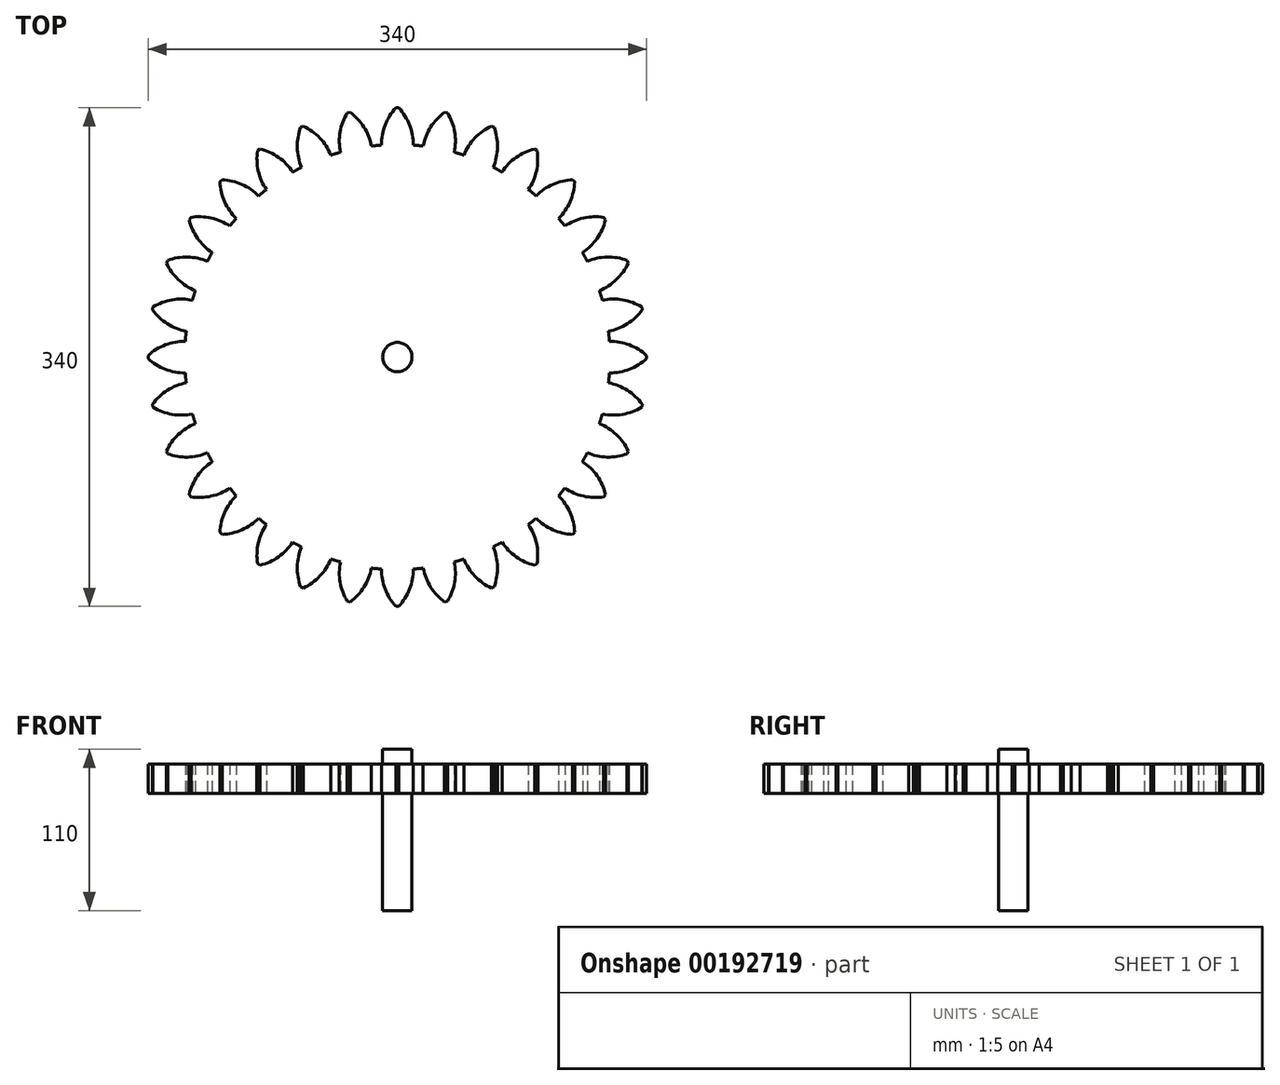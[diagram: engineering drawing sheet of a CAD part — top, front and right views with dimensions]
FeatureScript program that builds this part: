
annotation { "Feature Type Name" : "Feature", "Feature Type Description" : "" }
export const myFeature = defineFeature(function(context is Context, id is Id, definition is map)
    precondition{}
    {
        {
            var Q0;
            Q0=qCreatedBy(makeId("Top.planeOp"),FACE);
            var sketch = newSketch(context, id + "F0", { "sketchPlane" : qUnion([Q0])});
            skCircle(sketch, "E0", {"center": v(0, 0) * mm, "radius": 145 * mm});
            skLineSegment(sketch, "E1", {"start": v(0, 0) * mm, "end": v(0, 145) * mm, "construction": true});
            skLineSegment(sketch, "E2", {"start": v(0, 145) * mm, "end": v(0, 170) * mm});
            skLineSegment(sketch, "E3", {"start": v(0, 170) * mm, "end": v(-1, 170) * mm});
            skArc(sketch, "E4", {"start": v(-1, 170) * mm, "mid": v(-8.33, 158.24) * mm, "end": v(-10.8, 144.6) * mm});
            skLineSegment(sketch, "E5.MirrorCS", {"start": v(0, 170) * mm, "end": v(1, 170) * mm});
            skArc(sketch, "E6.MirrorCS", {"start": v(1, 170) * mm, "mid": v(8.33, 158.24) * mm, "end": v(10.8, 144.6) * mm});
            skArc(sketch, "E7.1.0", {"start": v(-34.15, 166.54) * mm, "mid": v(-39.04, 153.57) * mm, "end": v(-38.8, 139.71) * mm});
            skLineSegment(sketch, "E7.1.1", {"start": v(-33.17, 166.73) * mm, "end": v(-34.15, 166.54) * mm});
            skLineSegment(sketch, "E7.1.2", {"start": v(-33.17, 166.73) * mm, "end": v(-32.18, 166.93) * mm});
            skArc(sketch, "E7.1.3", {"start": v(-32.18, 166.93) * mm, "mid": v(-22.7, 156.82) * mm, "end": v(-17.62, 143.93) * mm});
            skArc(sketch, "E7.2.0", {"start": v(-65.98, 156.68) * mm, "mid": v(-68.25, 143) * mm, "end": v(-65.3, 129.46) * mm});
            skLineSegment(sketch, "E7.2.1", {"start": v(-65.06, 157.06) * mm, "end": v(-65.98, 156.68) * mm});
            skLineSegment(sketch, "E7.2.2", {"start": v(-65.06, 157.06) * mm, "end": v(-64.13, 157.44) * mm});
            skArc(sketch, "E7.2.3", {"start": v(-64.13, 157.44) * mm, "mid": v(-52.86, 149.38) * mm, "end": v(-45.36, 137.72) * mm});
            skArc(sketch, "E7.3.0", {"start": v(-95.28, 140.8) * mm, "mid": v(-94.84, 126.94) * mm, "end": v(-89.3, 114.23) * mm});
            skLineSegment(sketch, "E7.3.1", {"start": v(-94.45, 141.35) * mm, "end": v(-95.28, 140.8) * mm});
            skLineSegment(sketch, "E7.3.2", {"start": v(-94.45, 141.35) * mm, "end": v(-93.62, 141.9) * mm});
            skArc(sketch, "E7.3.3", {"start": v(-93.62, 141.9) * mm, "mid": v(-80.98, 136.2) * mm, "end": v(-71.36, 126.23) * mm});
            skArc(sketch, "E7.4.0", {"start": v(-120.92, 119.5) * mm, "mid": v(-117.78, 106) * mm, "end": v(-109.88, 94.61) * mm});
            skLineSegment(sketch, "E7.4.1", {"start": v(-120.2, 120.2) * mm, "end": v(-120.92, 119.5) * mm});
            skLineSegment(sketch, "E7.4.2", {"start": v(-120.2, 120.2) * mm, "end": v(-119.5, 120.92) * mm});
            skArc(sketch, "E7.4.3", {"start": v(-119.5, 120.92) * mm, "mid": v(-106, 117.78) * mm, "end": v(-94.61, 109.88) * mm});
            skArc(sketch, "E7.5.0", {"start": v(-141.9, 93.62) * mm, "mid": v(-136.2, 80.98) * mm, "end": v(-126.23, 71.36) * mm});
            skLineSegment(sketch, "E7.5.1", {"start": v(-141.35, 94.45) * mm, "end": v(-141.9, 93.62) * mm});
            skLineSegment(sketch, "E7.5.2", {"start": v(-141.35, 94.45) * mm, "end": v(-140.8, 95.28) * mm});
            skArc(sketch, "E7.5.3", {"start": v(-140.8, 95.28) * mm, "mid": v(-126.94, 94.84) * mm, "end": v(-114.23, 89.3) * mm});
            skArc(sketch, "E7.6.0", {"start": v(-157.44, 64.13) * mm, "mid": v(-149.38, 52.86) * mm, "end": v(-137.72, 45.36) * mm});
            skLineSegment(sketch, "E7.6.1", {"start": v(-157.06, 65.06) * mm, "end": v(-157.44, 64.13) * mm});
            skLineSegment(sketch, "E7.6.2", {"start": v(-157.06, 65.06) * mm, "end": v(-156.68, 65.98) * mm});
            skArc(sketch, "E7.6.3", {"start": v(-156.68, 65.98) * mm, "mid": v(-143, 68.25) * mm, "end": v(-129.46, 65.3) * mm});
            skArc(sketch, "E7.7.0", {"start": v(-166.93, 32.18) * mm, "mid": v(-156.82, 22.7) * mm, "end": v(-143.93, 17.62) * mm});
            skLineSegment(sketch, "E7.7.1", {"start": v(-166.73, 33.17) * mm, "end": v(-166.93, 32.18) * mm});
            skLineSegment(sketch, "E7.7.2", {"start": v(-166.73, 33.17) * mm, "end": v(-166.54, 34.15) * mm});
            skArc(sketch, "E7.7.3", {"start": v(-166.54, 34.15) * mm, "mid": v(-153.57, 39.04) * mm, "end": v(-139.71, 38.8) * mm});
            skArc(sketch, "E8.3.8.0", {"start": v(-170, -1) * mm, "mid": v(-158.24, -8.33) * mm, "end": v(-144.6, -10.8) * mm});
            skLineSegment(sketch, "E8.4.8.0", {"start": v(-170, 0) * mm, "end": v(-170, -1) * mm});
            skLineSegment(sketch, "E8.7.8.0", {"start": v(-170, 0) * mm, "end": v(-170, 1) * mm});
            skArc(sketch, "E8.10.8.0", {"start": v(-170, 1) * mm, "mid": v(-158.24, 8.33) * mm, "end": v(-144.6, 10.8) * mm});
            skArc(sketch, "E8.3.9.0", {"start": v(-166.54, -34.15) * mm, "mid": v(-153.57, -39.04) * mm, "end": v(-139.71, -38.8) * mm});
            skLineSegment(sketch, "E8.4.9.0", {"start": v(-166.73, -33.17) * mm, "end": v(-166.54, -34.15) * mm});
            skLineSegment(sketch, "E8.7.9.0", {"start": v(-166.73, -33.17) * mm, "end": v(-166.93, -32.18) * mm});
            skArc(sketch, "E8.10.9.0", {"start": v(-166.93, -32.18) * mm, "mid": v(-156.82, -22.7) * mm, "end": v(-143.93, -17.62) * mm});
            skArc(sketch, "E9.3.10.0", {"start": v(-156.68, -65.98) * mm, "mid": v(-143, -68.25) * mm, "end": v(-129.46, -65.3) * mm});
            skLineSegment(sketch, "E9.4.10.0", {"start": v(-157.06, -65.06) * mm, "end": v(-156.68, -65.98) * mm});
            skLineSegment(sketch, "E9.7.10.0", {"start": v(-157.06, -65.06) * mm, "end": v(-157.44, -64.13) * mm});
            skArc(sketch, "E9.10.10.0", {"start": v(-157.44, -64.13) * mm, "mid": v(-149.38, -52.86) * mm, "end": v(-137.72, -45.36) * mm});
            skArc(sketch, "E9.3.11.0", {"start": v(-140.8, -95.28) * mm, "mid": v(-126.94, -94.84) * mm, "end": v(-114.23, -89.3) * mm});
            skLineSegment(sketch, "E9.4.11.0", {"start": v(-141.35, -94.45) * mm, "end": v(-140.8, -95.28) * mm});
            skLineSegment(sketch, "E9.7.11.0", {"start": v(-141.35, -94.45) * mm, "end": v(-141.9, -93.62) * mm});
            skArc(sketch, "E9.10.11.0", {"start": v(-141.9, -93.62) * mm, "mid": v(-136.2, -80.98) * mm, "end": v(-126.23, -71.36) * mm});
            skArc(sketch, "E9.3.12.0", {"start": v(-119.5, -120.92) * mm, "mid": v(-106, -117.78) * mm, "end": v(-94.61, -109.88) * mm});
            skLineSegment(sketch, "E9.4.12.0", {"start": v(-120.2, -120.2) * mm, "end": v(-119.5, -120.92) * mm});
            skLineSegment(sketch, "E9.7.12.0", {"start": v(-120.2, -120.2) * mm, "end": v(-120.92, -119.5) * mm});
            skArc(sketch, "E9.10.12.0", {"start": v(-120.92, -119.5) * mm, "mid": v(-117.78, -106) * mm, "end": v(-109.88, -94.61) * mm});
            skArc(sketch, "E9.3.13.0", {"start": v(-93.62, -141.9) * mm, "mid": v(-80.98, -136.2) * mm, "end": v(-71.36, -126.23) * mm});
            skLineSegment(sketch, "E9.4.13.0", {"start": v(-94.45, -141.35) * mm, "end": v(-93.62, -141.9) * mm});
            skLineSegment(sketch, "E9.7.13.0", {"start": v(-94.45, -141.35) * mm, "end": v(-95.28, -140.8) * mm});
            skArc(sketch, "E9.10.13.0", {"start": v(-95.28, -140.8) * mm, "mid": v(-94.84, -126.94) * mm, "end": v(-89.3, -114.23) * mm});
            skArc(sketch, "E9.3.14.0", {"start": v(-64.13, -157.44) * mm, "mid": v(-52.86, -149.38) * mm, "end": v(-45.36, -137.72) * mm});
            skLineSegment(sketch, "E9.4.14.0", {"start": v(-65.06, -157.06) * mm, "end": v(-64.13, -157.44) * mm});
            skLineSegment(sketch, "E9.7.14.0", {"start": v(-65.06, -157.06) * mm, "end": v(-65.98, -156.68) * mm});
            skArc(sketch, "E9.10.14.0", {"start": v(-65.98, -156.68) * mm, "mid": v(-68.25, -143) * mm, "end": v(-65.3, -129.46) * mm});
            skArc(sketch, "E9.3.15.0", {"start": v(-32.18, -166.93) * mm, "mid": v(-22.7, -156.82) * mm, "end": v(-17.62, -143.93) * mm});
            skLineSegment(sketch, "E9.4.15.0", {"start": v(-33.17, -166.73) * mm, "end": v(-32.18, -166.93) * mm});
            skLineSegment(sketch, "E9.7.15.0", {"start": v(-33.17, -166.73) * mm, "end": v(-34.15, -166.54) * mm});
            skArc(sketch, "E9.10.15.0", {"start": v(-34.15, -166.54) * mm, "mid": v(-39.04, -153.57) * mm, "end": v(-38.8, -139.71) * mm});
            skArc(sketch, "E9.3.16.0", {"start": v(1, -170) * mm, "mid": v(8.33, -158.24) * mm, "end": v(10.8, -144.6) * mm});
            skLineSegment(sketch, "E9.4.16.0", {"start": v(0, -170) * mm, "end": v(1, -170) * mm});
            skLineSegment(sketch, "E9.7.16.0", {"start": v(0, -170) * mm, "end": v(-1, -170) * mm});
            skArc(sketch, "E9.10.16.0", {"start": v(-1, -170) * mm, "mid": v(-8.33, -158.24) * mm, "end": v(-10.8, -144.6) * mm});
            skArc(sketch, "E9.3.17.0", {"start": v(34.15, -166.54) * mm, "mid": v(39.04, -153.57) * mm, "end": v(38.8, -139.71) * mm});
            skLineSegment(sketch, "E9.4.17.0", {"start": v(33.17, -166.73) * mm, "end": v(34.15, -166.54) * mm});
            skLineSegment(sketch, "E9.7.17.0", {"start": v(33.17, -166.73) * mm, "end": v(32.18, -166.93) * mm});
            skArc(sketch, "E9.10.17.0", {"start": v(32.18, -166.93) * mm, "mid": v(22.7, -156.82) * mm, "end": v(17.62, -143.93) * mm});
            skArc(sketch, "E9.3.18.0", {"start": v(65.98, -156.68) * mm, "mid": v(68.25, -143) * mm, "end": v(65.3, -129.46) * mm});
            skLineSegment(sketch, "E9.4.18.0", {"start": v(65.06, -157.06) * mm, "end": v(65.98, -156.68) * mm});
            skLineSegment(sketch, "E9.7.18.0", {"start": v(65.06, -157.06) * mm, "end": v(64.13, -157.44) * mm});
            skArc(sketch, "E9.10.18.0", {"start": v(64.13, -157.44) * mm, "mid": v(52.86, -149.38) * mm, "end": v(45.36, -137.72) * mm});
            skArc(sketch, "E9.3.19.0", {"start": v(95.28, -140.8) * mm, "mid": v(94.84, -126.94) * mm, "end": v(89.3, -114.23) * mm});
            skLineSegment(sketch, "E9.4.19.0", {"start": v(94.45, -141.35) * mm, "end": v(95.28, -140.8) * mm});
            skLineSegment(sketch, "E9.7.19.0", {"start": v(94.45, -141.35) * mm, "end": v(93.62, -141.9) * mm});
            skArc(sketch, "E9.10.19.0", {"start": v(93.62, -141.9) * mm, "mid": v(80.98, -136.2) * mm, "end": v(71.36, -126.23) * mm});
            skArc(sketch, "E9.3.20.0", {"start": v(120.92, -119.5) * mm, "mid": v(117.78, -106) * mm, "end": v(109.88, -94.61) * mm});
            skLineSegment(sketch, "E9.4.20.0", {"start": v(120.2, -120.2) * mm, "end": v(120.92, -119.5) * mm});
            skLineSegment(sketch, "E9.7.20.0", {"start": v(120.2, -120.2) * mm, "end": v(119.5, -120.92) * mm});
            skArc(sketch, "E9.10.20.0", {"start": v(119.5, -120.92) * mm, "mid": v(106, -117.78) * mm, "end": v(94.61, -109.88) * mm});
            skArc(sketch, "E9.3.21.0", {"start": v(141.9, -93.62) * mm, "mid": v(136.2, -80.98) * mm, "end": v(126.23, -71.36) * mm});
            skLineSegment(sketch, "E9.4.21.0", {"start": v(141.35, -94.45) * mm, "end": v(141.9, -93.62) * mm});
            skLineSegment(sketch, "E9.7.21.0", {"start": v(141.35, -94.45) * mm, "end": v(140.8, -95.28) * mm});
            skArc(sketch, "E9.10.21.0", {"start": v(140.8, -95.28) * mm, "mid": v(126.94, -94.84) * mm, "end": v(114.23, -89.3) * mm});
            skArc(sketch, "E9.3.22.0", {"start": v(157.44, -64.13) * mm, "mid": v(149.38, -52.86) * mm, "end": v(137.72, -45.36) * mm});
            skLineSegment(sketch, "E9.4.22.0", {"start": v(157.06, -65.06) * mm, "end": v(157.44, -64.13) * mm});
            skLineSegment(sketch, "E9.7.22.0", {"start": v(157.06, -65.06) * mm, "end": v(156.68, -65.98) * mm});
            skArc(sketch, "E9.10.22.0", {"start": v(156.68, -65.98) * mm, "mid": v(143, -68.25) * mm, "end": v(129.46, -65.3) * mm});
            skArc(sketch, "E9.3.23.0", {"start": v(166.93, -32.18) * mm, "mid": v(156.82, -22.7) * mm, "end": v(143.93, -17.62) * mm});
            skLineSegment(sketch, "E9.4.23.0", {"start": v(166.73, -33.17) * mm, "end": v(166.93, -32.18) * mm});
            skLineSegment(sketch, "E9.7.23.0", {"start": v(166.73, -33.17) * mm, "end": v(166.54, -34.15) * mm});
            skArc(sketch, "E9.10.23.0", {"start": v(166.54, -34.15) * mm, "mid": v(153.57, -39.04) * mm, "end": v(139.71, -38.8) * mm});
            skArc(sketch, "E9.3.24.0", {"start": v(170, 1) * mm, "mid": v(158.24, 8.33) * mm, "end": v(144.6, 10.8) * mm});
            skLineSegment(sketch, "E9.4.24.0", {"start": v(170, 0) * mm, "end": v(170, 1) * mm});
            skLineSegment(sketch, "E9.7.24.0", {"start": v(170, 0) * mm, "end": v(170, -1) * mm});
            skArc(sketch, "E9.10.24.0", {"start": v(170, -1) * mm, "mid": v(158.24, -8.33) * mm, "end": v(144.6, -10.8) * mm});
            skArc(sketch, "E9.3.25.0", {"start": v(166.54, 34.15) * mm, "mid": v(153.57, 39.04) * mm, "end": v(139.71, 38.8) * mm});
            skLineSegment(sketch, "E9.4.25.0", {"start": v(166.73, 33.17) * mm, "end": v(166.54, 34.15) * mm});
            skLineSegment(sketch, "E9.7.25.0", {"start": v(166.73, 33.17) * mm, "end": v(166.93, 32.18) * mm});
            skArc(sketch, "E9.10.25.0", {"start": v(166.93, 32.18) * mm, "mid": v(156.82, 22.7) * mm, "end": v(143.93, 17.62) * mm});
            skArc(sketch, "E9.3.26.0", {"start": v(156.68, 65.98) * mm, "mid": v(143, 68.25) * mm, "end": v(129.46, 65.3) * mm});
            skLineSegment(sketch, "E9.4.26.0", {"start": v(157.06, 65.06) * mm, "end": v(156.68, 65.98) * mm});
            skLineSegment(sketch, "E9.7.26.0", {"start": v(157.06, 65.06) * mm, "end": v(157.44, 64.13) * mm});
            skArc(sketch, "E9.10.26.0", {"start": v(157.44, 64.13) * mm, "mid": v(149.38, 52.86) * mm, "end": v(137.72, 45.36) * mm});
            skArc(sketch, "E9.3.27.0", {"start": v(140.8, 95.28) * mm, "mid": v(126.94, 94.84) * mm, "end": v(114.23, 89.3) * mm});
            skLineSegment(sketch, "E9.4.27.0", {"start": v(141.35, 94.45) * mm, "end": v(140.8, 95.28) * mm});
            skLineSegment(sketch, "E9.7.27.0", {"start": v(141.35, 94.45) * mm, "end": v(141.9, 93.62) * mm});
            skArc(sketch, "E9.10.27.0", {"start": v(141.9, 93.62) * mm, "mid": v(136.2, 80.98) * mm, "end": v(126.23, 71.36) * mm});
            skArc(sketch, "E9.3.28.0", {"start": v(119.5, 120.92) * mm, "mid": v(106, 117.78) * mm, "end": v(94.61, 109.88) * mm});
            skLineSegment(sketch, "E9.4.28.0", {"start": v(120.2, 120.2) * mm, "end": v(119.5, 120.92) * mm});
            skLineSegment(sketch, "E9.7.28.0", {"start": v(120.2, 120.2) * mm, "end": v(120.92, 119.5) * mm});
            skArc(sketch, "E9.10.28.0", {"start": v(120.92, 119.5) * mm, "mid": v(117.78, 106) * mm, "end": v(109.88, 94.61) * mm});
            skArc(sketch, "E9.3.29.0", {"start": v(93.62, 141.9) * mm, "mid": v(80.98, 136.2) * mm, "end": v(71.36, 126.23) * mm});
            skLineSegment(sketch, "E9.4.29.0", {"start": v(94.45, 141.35) * mm, "end": v(93.62, 141.9) * mm});
            skLineSegment(sketch, "E9.7.29.0", {"start": v(94.45, 141.35) * mm, "end": v(95.28, 140.8) * mm});
            skArc(sketch, "E9.10.29.0", {"start": v(95.28, 140.8) * mm, "mid": v(94.84, 126.94) * mm, "end": v(89.3, 114.23) * mm});
            skArc(sketch, "E9.3.30.0", {"start": v(64.13, 157.44) * mm, "mid": v(52.86, 149.38) * mm, "end": v(45.36, 137.72) * mm});
            skLineSegment(sketch, "E9.4.30.0", {"start": v(65.06, 157.06) * mm, "end": v(64.13, 157.44) * mm});
            skLineSegment(sketch, "E9.7.30.0", {"start": v(65.06, 157.06) * mm, "end": v(65.98, 156.68) * mm});
            skArc(sketch, "E9.10.30.0", {"start": v(65.98, 156.68) * mm, "mid": v(68.25, 143) * mm, "end": v(65.3, 129.46) * mm});
            skArc(sketch, "E9.3.31.0", {"start": v(32.18, 166.93) * mm, "mid": v(22.7, 156.82) * mm, "end": v(17.62, 143.93) * mm});
            skLineSegment(sketch, "E9.4.31.0", {"start": v(33.17, 166.73) * mm, "end": v(32.18, 166.93) * mm});
            skLineSegment(sketch, "E9.7.31.0", {"start": v(33.17, 166.73) * mm, "end": v(34.15, 166.54) * mm});
            skArc(sketch, "E9.10.31.0", {"start": v(34.15, 166.54) * mm, "mid": v(39.04, 153.57) * mm, "end": v(38.8, 139.71) * mm});
            skSolve(sketch);
        }
        {
            var Q0;
            Q0=qSketchRegion(id+"F0",true);
            extrude(context, id + "F1", {"entities" : qUnion([Q0]), "depth" : 20 * mm});
        }
        {
            var Q0;
            Q0=makeQuery(id+"F1.opExtrude","CAP_FACE",FACE,{"disambiguationData":[OSD([sQuery(id+"F0.wireOp",EDGE,"E0"),sQuery(id+"F0.wireOp",EDGE,"E3"),sQuery(id+"F0.wireOp",EDGE,"E4"),sQuery(id+"F0.wireOp",EDGE,"E5.MirrorCS"),sQuery(id+"F0.wireOp",EDGE,"E6.MirrorCS"),sQuery(id+"F0.wireOp",EDGE,"E7.1.0"),sQuery(id+"F0.wireOp",EDGE,"E7.1.1"),sQuery(id+"F0.wireOp",EDGE,"E7.1.2"),sQuery(id+"F0.wireOp",EDGE,"E7.1.3"),sQuery(id+"F0.wireOp",EDGE,"E7.2.0"),sQuery(id+"F0.wireOp",EDGE,"E7.2.1"),sQuery(id+"F0.wireOp",EDGE,"E7.2.2"),sQuery(id+"F0.wireOp",EDGE,"E7.2.3"),sQuery(id+"F0.wireOp",EDGE,"E7.3.0"),sQuery(id+"F0.wireOp",EDGE,"E7.3.1"),sQuery(id+"F0.wireOp",EDGE,"E7.3.2"),sQuery(id+"F0.wireOp",EDGE,"E7.3.3"),sQuery(id+"F0.wireOp",EDGE,"E7.4.0"),sQuery(id+"F0.wireOp",EDGE,"E7.4.1"),sQuery(id+"F0.wireOp",EDGE,"E7.4.2"),sQuery(id+"F0.wireOp",EDGE,"E7.4.3"),sQuery(id+"F0.wireOp",EDGE,"E7.5.0"),sQuery(id+"F0.wireOp",EDGE,"E7.5.1"),sQuery(id+"F0.wireOp",EDGE,"E7.5.2"),sQuery(id+"F0.wireOp",EDGE,"E7.5.3"),sQuery(id+"F0.wireOp",EDGE,"E7.6.0"),sQuery(id+"F0.wireOp",EDGE,"E7.6.1"),sQuery(id+"F0.wireOp",EDGE,"E7.6.2"),sQuery(id+"F0.wireOp",EDGE,"E7.6.3"),sQuery(id+"F0.wireOp",EDGE,"E7.7.0"),sQuery(id+"F0.wireOp",EDGE,"E7.7.1"),sQuery(id+"F0.wireOp",EDGE,"E7.7.2"),sQuery(id+"F0.wireOp",EDGE,"E7.7.3"),sQuery(id+"F0.wireOp",EDGE,"E7.8.0"),sQuery(id+"F0.wireOp",EDGE,"E7.8.1"),sQuery(id+"F0.wireOp",EDGE,"E7.8.2"),sQuery(id+"F0.wireOp",EDGE,"E7.8.3"),sQuery(id+"F0.wireOp",EDGE,"E7.9.0"),sQuery(id+"F0.wireOp",EDGE,"E7.9.1"),sQuery(id+"F0.wireOp",EDGE,"E7.9.2"),sQuery(id+"F0.wireOp",EDGE,"E7.9.3"),sQuery(id+"F0.wireOp",EDGE,"E7.10.0"),sQuery(id+"F0.wireOp",EDGE,"E7.10.1"),sQuery(id+"F0.wireOp",EDGE,"E7.10.2"),sQuery(id+"F0.wireOp",EDGE,"E7.10.3"),sQuery(id+"F0.wireOp",EDGE,"E7.11.0"),sQuery(id+"F0.wireOp",EDGE,"E7.11.1"),sQuery(id+"F0.wireOp",EDGE,"E7.11.2"),sQuery(id+"F0.wireOp",EDGE,"E7.11.3"),sQuery(id+"F0.wireOp",EDGE,"E7.12.0"),sQuery(id+"F0.wireOp",EDGE,"E7.12.1"),sQuery(id+"F0.wireOp",EDGE,"E7.12.2"),sQuery(id+"F0.wireOp",EDGE,"E7.12.3"),sQuery(id+"F0.wireOp",EDGE,"E7.13.0"),sQuery(id+"F0.wireOp",EDGE,"E7.13.1"),sQuery(id+"F0.wireOp",EDGE,"E7.13.2"),sQuery(id+"F0.wireOp",EDGE,"E7.13.3"),sQuery(id+"F0.wireOp",EDGE,"E7.14.0"),sQuery(id+"F0.wireOp",EDGE,"E7.14.1"),sQuery(id+"F0.wireOp",EDGE,"E7.14.2"),sQuery(id+"F0.wireOp",EDGE,"E7.14.3"),sQuery(id+"F0.wireOp",EDGE,"E7.15.0"),sQuery(id+"F0.wireOp",EDGE,"E7.15.1"),sQuery(id+"F0.wireOp",EDGE,"E7.15.2"),sQuery(id+"F0.wireOp",EDGE,"E7.15.3")])],"isStart":false});
            var sketch = newSketch(context, id + "F2", { "sketchPlane" : qUnion([Q0])});
            skCircle(sketch, "E10", {"center": v(0, 0) * mm, "radius": 10 * mm});
            skSolve(sketch);
        }
        {
            var Q0;
            Q0=qSketchRegion(id+"F2",true);
            extrude(context, id + "F3", {"entities" : qUnion([Q0]), "operationType" : NewBodyOperationType.ADD, "depth" : 10 * mm, "hasSecondDirection" : true, "secondDirectionOppositeDirection" : true, "secondDirectionDepth" : 100 * mm});
        }
    });
